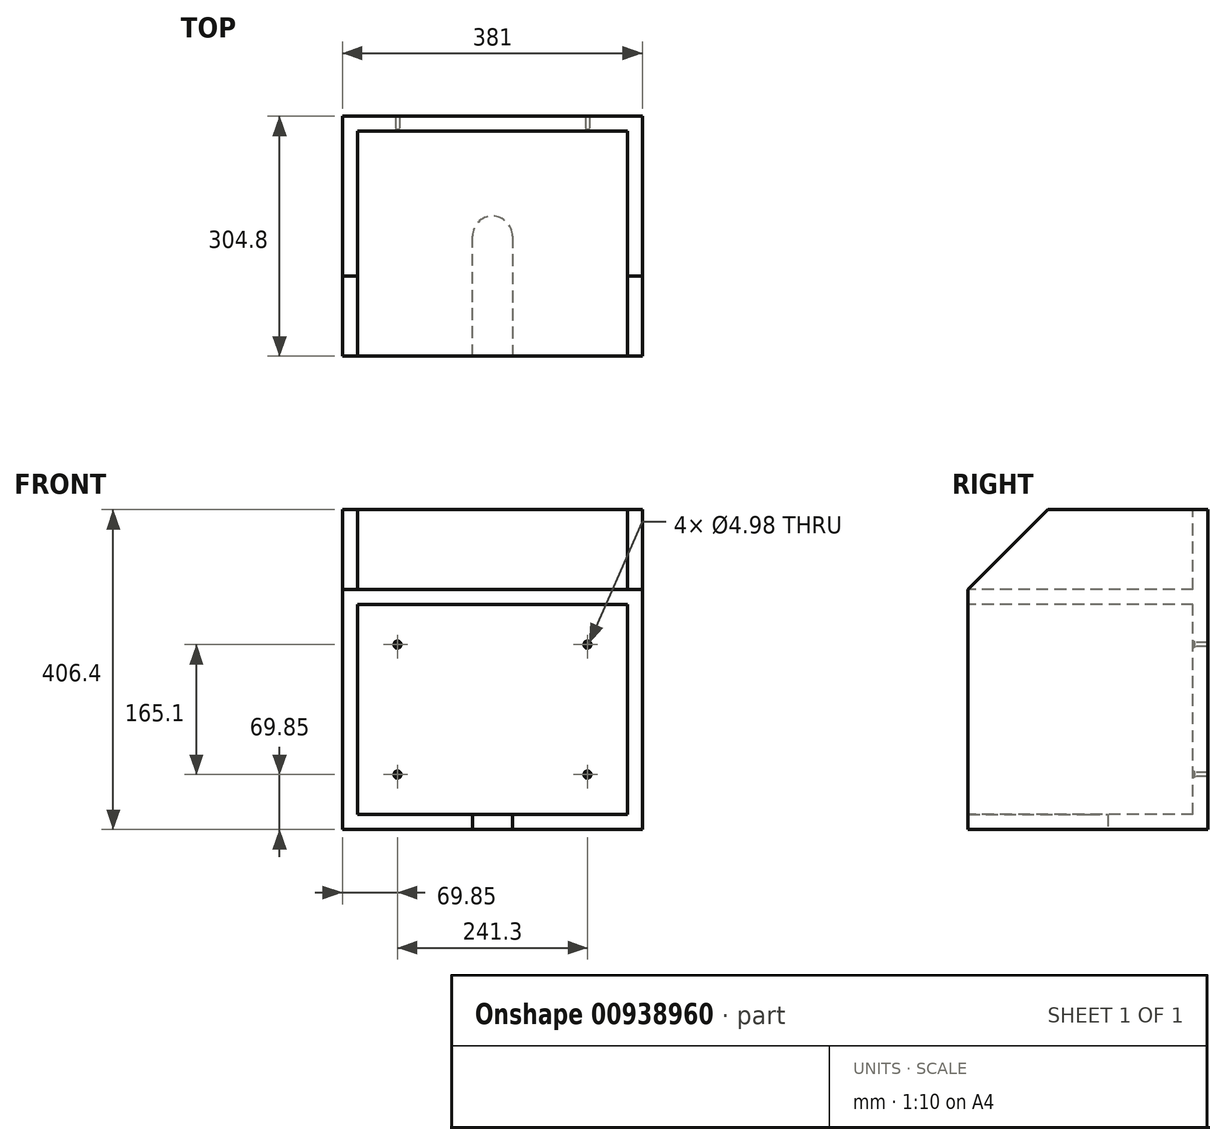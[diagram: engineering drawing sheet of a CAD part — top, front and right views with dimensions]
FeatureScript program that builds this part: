
annotation { "Feature Type Name" : "Feature", "Feature Type Description" : "" }
export const myFeature = defineFeature(function(context is Context, id is Id, definition is map)
    precondition{}
    {
        {
            var Q0;
            Q0=qCreatedBy(makeId("Right.planeOp"),FACE);
            var sketch = newSketch(context, id + "F0", { "sketchPlane" : qUnion([Q0])});
            skLineSegment(sketch, "E0", {"start": v(0, 0) * mm, "end": v(304.8, 0) * mm});
            skLineSegment(sketch, "E1", {"start": v(304.8, 0) * mm, "end": v(304.8, 406.4) * mm});
            skLineSegment(sketch, "E2", {"start": v(304.8, 406.4) * mm, "end": v(101.6, 406.4) * mm});
            skLineSegment(sketch, "E3", {"start": v(101.6, 406.4) * mm, "end": v(0, 304.8) * mm});
            skLineSegment(sketch, "E4", {"start": v(0, 304.8) * mm, "end": v(0, 0) * mm});
            skSolve(sketch);
        }
        {
            var Q0;
            Q0 = qSketchRegion(id + "F0", true);
            extrude(context, id + "F1", {"entities" : qUnion([Q0]), "endBound" : BoundingType.SYMMETRIC, "depth" : 381 * mm, "offsetDistance" : 25.4 * mm});
        }
        {
            var Q0;
            Q0=makeQuery(id+"F1.opExtrude","SWEPT_FACE",FACE,{"disambiguationData":[OSD([sQuery(id+"F0.wireOp",EDGE,"E4")])]});
            var sketch = newSketch(context, id + "F2", { "sketchPlane" : qUnion([Q0])});
            skLineSegment(sketch, "E5.bottom", {"start": v(171.45, 406.4) * mm, "end": v(-171.45, 406.4) * mm});
            skLineSegment(sketch, "E5.top", {"start": v(171.45, 304.8) * mm, "end": v(-171.45, 304.8) * mm});
            skLineSegment(sketch, "E5.left", {"start": v(171.45, 406.4) * mm, "end": v(171.45, 304.8) * mm});
            skLineSegment(sketch, "E5.right", {"start": v(-171.45, 406.4) * mm, "end": v(-171.45, 304.8) * mm});
            skSolve(sketch);
        }
        {
            var Q0;
            Q0 = qSketchRegion(id + "F2", true);
            var Q1;
            Q1=makeQuery(id+"F1.opExtrude","SWEPT_FACE",FACE,{"disambiguationData":[OSD([sQuery(id+"F0.wireOp",EDGE,"E1")])]});
            extrude(context, id + "F3", {"entities" : qUnion([Q0]), "operationType" : NewBodyOperationType.REMOVE, "endBound" : BoundingType.UP_TO_SURFACE, "oppositeDirection" : true, "depth" : 25.4 * mm, "endBoundEntityFace" : qUnion([Q1]), "hasOffset" : true, "offsetDistance" : 19.05 * mm});
        }
        {
            var Q0;
            Q0=makeQuery(id+"F1.opExtrude","SWEPT_FACE",FACE,{"disambiguationData":[OSD([sQuery(id+"F0.wireOp",EDGE,"E4")])]});
            var sketch = newSketch(context, id + "F4", { "sketchPlane" : qUnion([Q0])});
            skLineSegment(sketch, "E6.bottom", {"start": v(171.45, 285.75) * mm, "end": v(-171.45, 285.75) * mm});
            skLineSegment(sketch, "E6.top", {"start": v(171.45, 19.05) * mm, "end": v(-171.45, 19.05) * mm});
            skLineSegment(sketch, "E6.left", {"start": v(171.45, 285.75) * mm, "end": v(171.45, 19.05) * mm});
            skLineSegment(sketch, "E6.right", {"start": v(-171.45, 285.75) * mm, "end": v(-171.45, 19.05) * mm});
            skSolve(sketch);
        }
        {
            var Q0;
            Q0 = qSketchRegion(id + "F4", true);
            var Q1;
            Q1=makeQuery(id+"F1.opExtrude","SWEPT_FACE",FACE,{"disambiguationData":[OSD([sQuery(id+"F0.wireOp",EDGE,"E1")])]});
            extrude(context, id + "F5", {"entities" : qUnion([Q0]), "operationType" : NewBodyOperationType.REMOVE, "endBound" : BoundingType.UP_TO_SURFACE, "oppositeDirection" : true, "depth" : 25.4 * mm, "endBoundEntityFace" : qUnion([Q1]), "hasOffset" : true, "offsetDistance" : 19.05 * mm});
        }
        {
            var Q0;
            Q0=makeQuery(id+"F1.opExtrude","SWEPT_FACE",FACE,{"disambiguationData":[OSD([sQuery(id+"F0.wireOp",EDGE,"E0")])]});
            var sketch = newSketch(context, id + "F6", { "sketchPlane" : qUnion([Q0])});
            skLineSegment(sketch, "E7", {"start": v(-25.4, 0) * mm, "end": v(-25.4, -152.4) * mm});
            skArc(sketch, "E8", {"start": v(-25.4, -152.4) * mm, "mid": v(0, -177.8) * mm, "end": v(25.4, -152.4) * mm});
            skLineSegment(sketch, "E9", {"start": v(25.4, -152.4) * mm, "end": v(25.4, 0) * mm});
            skLineSegment(sketch, "E10", {"start": v(25.4, 0) * mm, "end": v(-25.4, 0) * mm});
            skSolve(sketch);
        }
        {
            var Q0;
            Q0 = qSketchRegion(id + "F6", true);
            extrude(context, id + "F7", {"entities" : qUnion([Q0]), "operationType" : NewBodyOperationType.REMOVE, "endBound" : BoundingType.UP_TO_NEXT, "oppositeDirection" : true, "depth" : 25.4 * mm, "offsetDistance" : 25.4 * mm});
        }
        {
            var Q0;
            Q0=makeQuery(id+"F5.boolean.opBoolean","COPY",FACE,{"derivedFrom":makeQuery(id+"F5.opExtrude","CAP_FACE",FACE,{"disambiguationData":[OSD([sQuery(id+"F4.wireOp",EDGE,"E6.bottom"),sQuery(id+"F4.wireOp",EDGE,"E6.top"),sQuery(id+"F4.wireOp",EDGE,"E6.left"),sQuery(id+"F4.wireOp",EDGE,"E6.right")])],"isStart":false})});
            var sketch = newSketch(context, id + "F8", { "sketchPlane" : qUnion([Q0])});
            skPoint(sketch, "E11", {"position": v(120.65, 234.95) * mm});
            skPoint(sketch, "E12", {"position": v(-120.65, 234.95) * mm});
            skPoint(sketch, "E13", {"position": v(-120.65, 69.85) * mm});
            skPoint(sketch, "E14", {"position": v(120.65, 69.85) * mm});
            skSolve(sketch);
        }
        {
            var Q0;
            Q0=sQuery(id+"F8.wireOp",VERTEX,"E14");
            var Q1;
            Q1=sQuery(id+"F8.wireOp",VERTEX,"E11");
            var Q2;
            Q2=sQuery(id+"F8.wireOp",VERTEX,"E12");
            var Q3;
            Q3=sQuery(id+"F8.wireOp",VERTEX,"E13");
            var Q4;
            Q4=makeQuery(id+"F1.opExtrude","SWEPT_BODY",BODY,{"disambiguationData":[OSD([sQuery(id+"F0.wireOp",EDGE,"E0"),sQuery(id+"F0.wireOp",EDGE,"E1"),sQuery(id+"F0.wireOp",EDGE,"E2"),sQuery(id+"F0.wireOp",EDGE,"E3"),sQuery(id+"F0.wireOp",EDGE,"E4")])]});
            hole(context, id + "F9", {"style" : HoleStyle.C_SINK, "endStyle" : HoleEndStyle.THROUGH, "standardTappedOrClearance" : lookupTablePath({ "standard" : "ANSI", "fit" : "Normal (ASME)", "size" : "#8", "type" : "Clearance" }), "standardBlindInLast" : lookupTablePath({ "fit" : "Normal", "standard" : "ANSI", "engagement" : "75%", "pitch" : "32 tpi", "size" : "#8", "type" : "Clearance & tapped" }), "holeDiameter" : 4.98 * mm, "cSinkDiameter" : 9.12 * mm, "cSinkAngle" : 82 * degree, "majorDiameter" : 6.35 * mm, "isTappedThrough" : true, "tappedDepth" : 12.7 * mm, "tapClearance" : 3, "locations" : qUnion([Q0, Q1, Q2, Q3]), "scope" : qUnion([Q4])});
        }
    });
